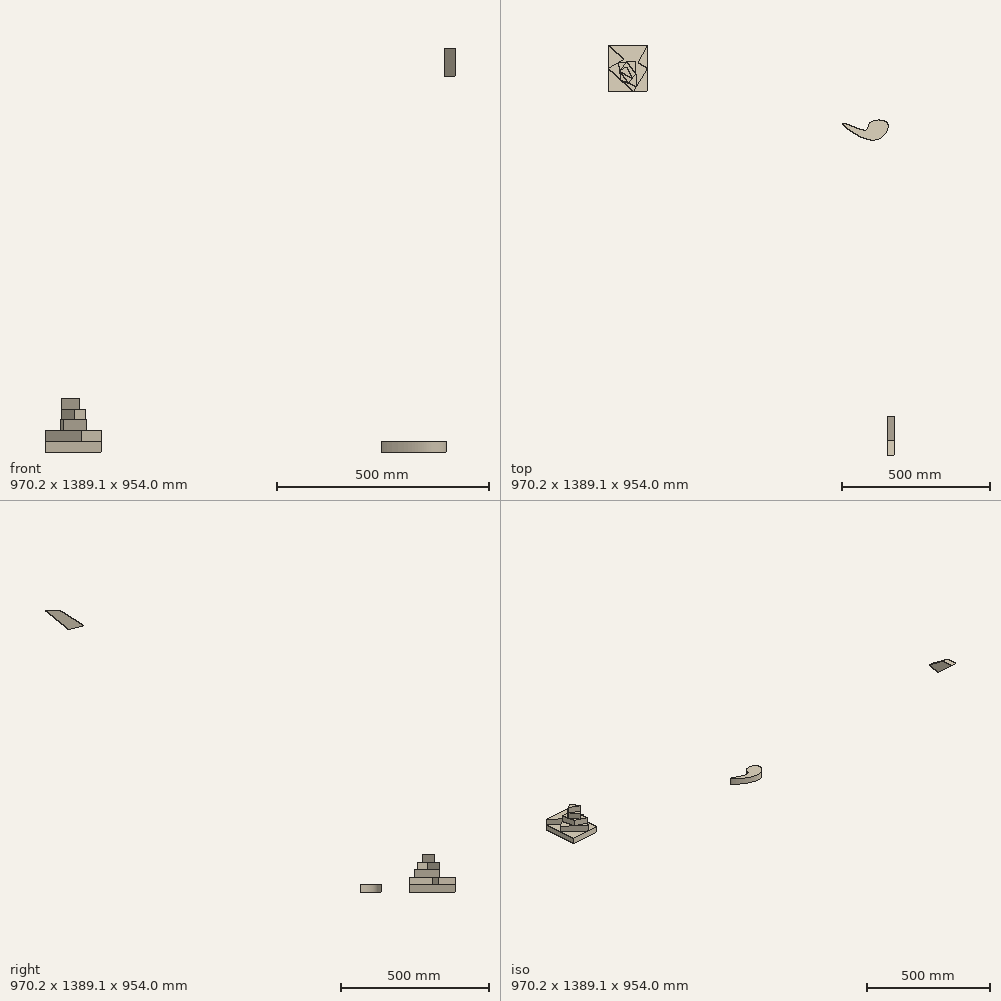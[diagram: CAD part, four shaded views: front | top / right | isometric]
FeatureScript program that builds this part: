
annotation { "Feature Type Name" : "Feature", "Feature Type Description" : "" }
export const myFeature = defineFeature(function(context is Context, id is Id, definition is map)
    precondition{}
    {
        {
            var Q0;
            Q0=qCreatedBy(makeId("Top.planeOp"),FACE);
            var sketch = newSketch(context, id + "F0", { "sketchPlane" : qUnion([Q0])});
            skFitSpline(sketch, "E0", {"points": [v(-58.6, 0) * mm, v(0, 0) * mm, v(-43.3, -58.06) * mm, v(-150.34, 0) * mm, v(-71.62, -24.12) * mm, v(-58.6, 0) * mm]});
            skLineSegment(sketch, "E1.bottom", {"start": v(-944.81, 262.83) * mm, "end": v(-811.38, 262.83) * mm});
            skLineSegment(sketch, "E1.top", {"start": v(-944.81, 106.2) * mm, "end": v(-811.38, 106.2) * mm});
            skLineSegment(sketch, "E1.left", {"start": v(-944.81, 262.83) * mm, "end": v(-944.81, 106.2) * mm});
            skLineSegment(sketch, "E1.right", {"start": v(-811.38, 262.83) * mm, "end": v(-811.38, 106.2) * mm});
            skSolve(sketch);
        }
        {
            var Q0;
            Q0 = qSketchRegion(id + "F0", true);
            var Q1;
            Q1=makeQuery(id+"F0.imprint","IMPRINT",FACE,{"disambiguationData":[TD([[makeQuery(id+"F0.imprint","IMPRINT",EDGE,{"derivedFrom":sQuery(id+"F0.wireOp",EDGE,"E1.bottom")}),-1.0]])]});
            extrude(context, id + "F1", {"entities" : qUnion([Q0, Q1]), "depth" : 25.4 * mm, "offsetDistance" : 25.4 * mm});
        }
        {
            var Q0;
            Q0=makeQuery(id+"F1.opExtrude","CAP_FACE",FACE,{"disambiguationData":[OSD([sQuery(id+"F0.wireOp",EDGE,"E1.bottom"),sQuery(id+"F0.wireOp",EDGE,"E1.top"),sQuery(id+"F0.wireOp",EDGE,"E1.left"),sQuery(id+"F0.wireOp",EDGE,"E1.right")])],"isStart":false});
            var sketch = newSketch(context, id + "F2", { "sketchPlane" : qUnion([Q0])});
            skLineSegment(sketch, "E2", {"start": v(-875.92, 223.7) * mm, "end": v(-811.38, 184.52) * mm});
            skLineSegment(sketch, "E3", {"start": v(-811.38, 184.52) * mm, "end": v(-858.93, 106.2) * mm});
            skLineSegment(sketch, "E4", {"start": v(-858.93, 106.2) * mm, "end": v(-944.81, 184.52) * mm});
            skLineSegment(sketch, "E5", {"start": v(-944.81, 184.52) * mm, "end": v(-875.92, 223.7) * mm});
            skSolve(sketch);
        }
        {
            var Q0;
            Q0=makeQuery(id+"F2.imprint","IMPRINT",FACE,{"disambiguationData":[TD([[makeQuery(id+"F2.imprint","IMPRINT",EDGE,{"derivedFrom":sQuery(id+"F2.wireOp",EDGE,"E2")}),-1.0]])]});
            extrude(context, id + "F3", {"entities" : qUnion([Q0]), "operationType" : NewBodyOperationType.ADD, "depth" : 25.4 * mm, "offsetDistance" : 25.4 * mm});
        }
        {
            var Q0;
            Q0=qCreatedBy(makeId("Right.planeOp"),FACE);
            var sketch = newSketch(context, id + "F4", { "sketchPlane" : qUnion([Q0])});
            skLineSegment(sketch, "E6", {"start": v(-1047.25, 889.75) * mm, "end": v(-1126.26, 954) * mm});
            skLineSegment(sketch, "E7", {"start": v(-1126.26, 954) * mm, "end": v(-1075.34, 954) * mm});
            skLineSegment(sketch, "E8", {"start": v(-1075.34, 954) * mm, "end": v(-995.22, 902.9) * mm});
            skLineSegment(sketch, "E9", {"start": v(-995.22, 902.9) * mm, "end": v(-1047.25, 889.75) * mm});
            skSolve(sketch);
        }
        {
            var Q0;
            Q0=makeQuery(id+"F4.imprint","IMPRINT",FACE,{"disambiguationData":[TD([[makeQuery(id+"F4.imprint","IMPRINT",EDGE,{"derivedFrom":sQuery(id+"F4.wireOp",EDGE,"E6")}),-1.0]])]});
            extrude(context, id + "F5", {"entities" : qUnion([Q0]), "depth" : 25.4 * mm, "offsetDistance" : 25.4 * mm});
        }
        {
            var Q0;
            Q0=makeQuery(id+"F3.opExtrude","CAP_FACE",FACE,{"disambiguationData":[OSD([sQuery(id+"F2.wireOp",EDGE,"E2"),sQuery(id+"F2.wireOp",EDGE,"E3"),sQuery(id+"F2.wireOp",EDGE,"E4"),sQuery(id+"F2.wireOp",EDGE,"E5")])],"isStart":false});
            var sketch = newSketch(context, id + "F6", { "sketchPlane" : qUnion([Q0])});
            skLineSegment(sketch, "E10", {"start": v(-853.6, 210.15) * mm, "end": v(-848.74, 122.98) * mm});
            skLineSegment(sketch, "E11", {"start": v(-848.74, 122.98) * mm, "end": v(-901.87, 145.36) * mm});
            skLineSegment(sketch, "E12", {"start": v(-901.87, 145.36) * mm, "end": v(-910.37, 204.1) * mm});
            skLineSegment(sketch, "E13", {"start": v(-910.37, 204.1) * mm, "end": v(-853.6, 210.15) * mm});
            skSolve(sketch);
        }
        {
            var Q0;
            Q0=makeQuery(id+"F6.imprint","IMPRINT",FACE,{"disambiguationData":[TD([[makeQuery(id+"F6.imprint","IMPRINT",EDGE,{"derivedFrom":sQuery(id+"F6.wireOp",EDGE,"E10")}),-1.0]])]});
            extrude(context, id + "F7", {"entities" : qUnion([Q0]), "operationType" : NewBodyOperationType.ADD, "depth" : 25.4 * mm, "offsetDistance" : 25.4 * mm});
        }
        {
            var Q0;
            Q0=makeQuery(id+"F7.opExtrude","CAP_FACE",FACE,{"disambiguationData":[OSD([sQuery(id+"F6.wireOp",EDGE,"E10"),sQuery(id+"F6.wireOp",EDGE,"E11"),sQuery(id+"F6.wireOp",EDGE,"E12"),sQuery(id+"F6.wireOp",EDGE,"E13")])],"isStart":false});
            var sketch = newSketch(context, id + "F8", { "sketchPlane" : qUnion([Q0])});
            skLineSegment(sketch, "E14", {"start": v(-851.17, 166.56) * mm, "end": v(-881.98, 207.13) * mm});
            skLineSegment(sketch, "E15", {"start": v(-881.98, 207.13) * mm, "end": v(-906.12, 174.73) * mm});
            skLineSegment(sketch, "E16", {"start": v(-906.12, 174.73) * mm, "end": v(-875.3, 134.17) * mm});
            skLineSegment(sketch, "E17", {"start": v(-875.3, 134.17) * mm, "end": v(-851.17, 166.56) * mm});
            skSolve(sketch);
        }
        {
            var Q0;
            Q0=makeQuery(id+"F8.imprint","IMPRINT",FACE,{"disambiguationData":[TD([[makeQuery(id+"F8.imprint","IMPRINT",EDGE,{"derivedFrom":sQuery(id+"F8.wireOp",EDGE,"E14")}),1.0]])]});
            extrude(context, id + "F9", {"entities" : qUnion([Q0]), "operationType" : NewBodyOperationType.ADD, "depth" : 25.4 * mm, "offsetDistance" : 25.4 * mm});
        }
        {
            var Q0;
            Q0=makeQuery(id+"F9.opExtrude","CAP_FACE",FACE,{"disambiguationData":[OSD([sQuery(id+"F8.wireOp",EDGE,"E14"),sQuery(id+"F8.wireOp",EDGE,"E15"),sQuery(id+"F8.wireOp",EDGE,"E16"),sQuery(id+"F8.wireOp",EDGE,"E17")])],"isStart":false});
            var sketch = newSketch(context, id + "F10", { "sketchPlane" : qUnion([Q0])});
            skLineSegment(sketch, "E18", {"start": v(-863.24, 150.37) * mm, "end": v(-881.98, 190.93) * mm});
            skPoint(sketch, "E18.endSnap0", {"position": v(-894.05, 190.93) * mm});
            skLineSegment(sketch, "E19", {"start": v(-881.98, 190.93) * mm, "end": v(-906.12, 174.73) * mm});
            skLineSegment(sketch, "E20", {"start": v(-906.12, 174.73) * mm, "end": v(-863.24, 150.37) * mm});
            skSolve(sketch);
        }
        {
            var Q0;
            Q0=makeQuery(id+"F10.imprint","IMPRINT",FACE,{"disambiguationData":[TD([[makeQuery(id+"F10.imprint","IMPRINT",EDGE,{"derivedFrom":sQuery(id+"F10.wireOp",EDGE,"E18")}),1.0]])]});
            extrude(context, id + "F11", {"entities" : qUnion([Q0]), "operationType" : NewBodyOperationType.ADD, "depth" : 25.4 * mm, "offsetDistance" : 25.4 * mm});
        }
        {
            var Q0;
            {var subQ0=sQuery(id+"F0.wireOp",EDGE,"E1.left");var subQ1=sQuery(id+"F0.wireOp",EDGE,"E1.right");var subQ2=sQuery(id+"F0.wireOp",EDGE,"E1.bottom");var subQ3=makeQuery(id+"F1.opExtrude","CAP_FACE",FACE,{"disambiguationData":[OSD([subQ2,sQuery(id+"F0.wireOp",EDGE,"E1.top"),subQ0,subQ1])],"isStart":false});Q0=makeQuery(id+"F3.boolean.opBoolean","SPLIT",FACE,{"disambiguationData":[TD([makeQuery(id+"F1.opExtrude","SWEPT_FACE",FACE,{"disambiguationData":[OSD([subQ2])]}),subQ3,makeQuery(id+"F1.opExtrude","SWEPT_FACE",FACE,{"disambiguationData":[OSD([subQ0])]}),makeQuery(id+"F1.opExtrude","SWEPT_FACE",FACE,{"disambiguationData":[OSD([subQ1])]}),makeQuery(id+"F3.opExtrude","SWEPT_FACE",FACE,{"disambiguationData":[OSD([sQuery(id+"F2.wireOp",EDGE,"E2")])]}),makeQuery(id+"F3.opExtrude","SWEPT_FACE",FACE,{"disambiguationData":[OSD([sQuery(id+"F2.wireOp",EDGE,"E3")])]}),makeQuery(id+"F3.opExtrude","SWEPT_FACE",FACE,{"disambiguationData":[OSD([sQuery(id+"F2.wireOp",EDGE,"E4")])]}),makeQuery(id+"F3.opExtrude","SWEPT_FACE",FACE,{"disambiguationData":[OSD([sQuery(id+"F2.wireOp",EDGE,"E5")])]})])],"derivedFrom":subQ3});}
            var sketch = newSketch(context, id + "F12", { "sketchPlane" : qUnion([Q0])});
            skLineSegment(sketch, "E21", {"start": v(-854.19, 184.52) * mm, "end": v(-811.38, 262.83) * mm});
            skLineSegment(sketch, "E22", {"start": v(-811.38, 262.83) * mm, "end": v(-944.81, 262.83) * mm});
            skLineSegment(sketch, "E23", {"start": v(-944.81, 262.83) * mm, "end": v(-854.19, 184.52) * mm});
            skSolve(sketch);
        }
        {
            var Q0;
            {var subQ8=sQuery(id+"F12.wireOp",EDGE,"E22");Q0=makeQuery(id+"F12.imprint","IMPRINT",FACE,{"disambiguationData":[TD([[makeQuery(id+"F12.imprint","IMPRINT",EDGE,{"derivedFrom":subQ8}),-1.0]])]});}
            extrude(context, id + "F13", {"entities" : qUnion([Q0]), "operationType" : NewBodyOperationType.ADD, "depth" : 25.4 * mm, "offsetDistance" : 25.4 * mm});
        }
    });
